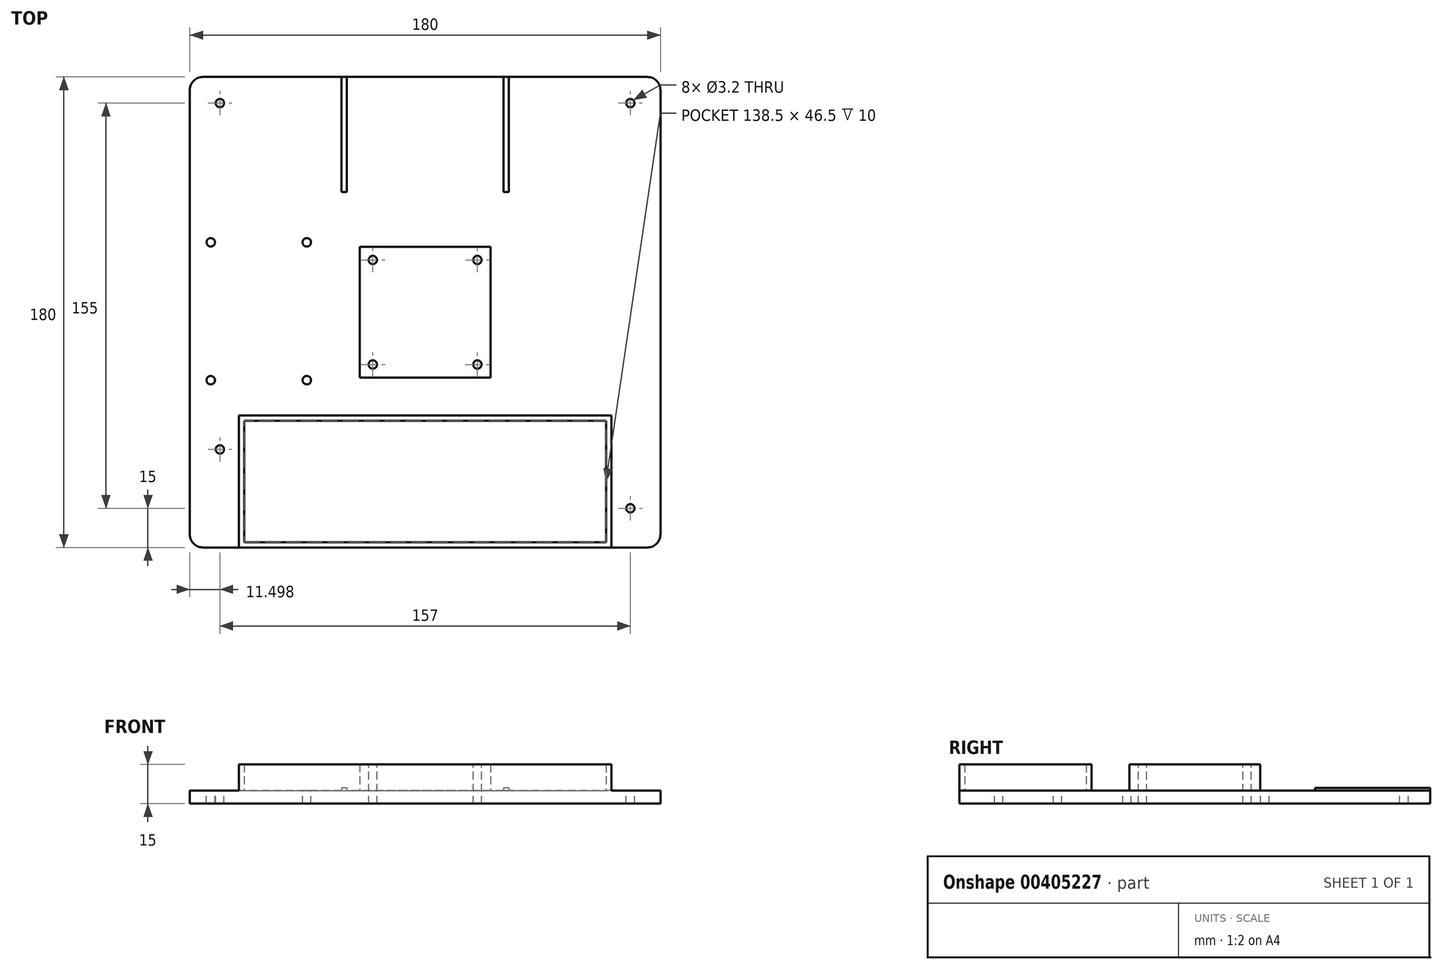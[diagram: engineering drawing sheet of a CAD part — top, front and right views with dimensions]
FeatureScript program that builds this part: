
annotation { "Feature Type Name" : "Feature", "Feature Type Description" : "" }
export const myFeature = defineFeature(function(context is Context, id is Id, definition is map)
    precondition{}
    {
        {
            var Q0;
            Q0=qCreatedBy(makeId("Top.planeOp"),FACE);
            var sketch = newSketch(context, id + "F0", { "sketchPlane" : qUnion([Q0])});
            skLineSegment(sketch, "E0.bottom", {"start": v(87.98, 0) * mm, "end": v(-92.02, 0) * mm});
            skLineSegment(sketch, "E0.top", {"start": v(87.98, 180) * mm, "end": v(-92.02, 180) * mm});
            skLineSegment(sketch, "E0.left", {"start": v(87.98, 0) * mm, "end": v(87.98, 180) * mm});
            skLineSegment(sketch, "E0.right", {"start": v(-92.02, 0) * mm, "end": v(-92.02, 180) * mm});
            skSolve(sketch);
        }
        {
            var Q0;
            Q0=makeQuery(id+"F0.imprint","IMPRINT",FACE,{"disambiguationData":[TD([[makeQuery(id+"F0.imprint","IMPRINT",EDGE,{"derivedFrom":sQuery(id+"F0.wireOp",EDGE,"E0.bottom")}),-1.0]])]});
            extrude(context, id + "F1", {"entities" : qUnion([Q0]), "depth" : 5 * mm});
        }
        {
            var Q0;
            Q0=makeQuery(id+"F1.opExtrude","SWEPT_EDGE",EDGE,{"disambiguationData":[OSD([sQuery(id+"F0.wireOp",EDGE,"E0.bottom"),sQuery(id+"F0.wireOp",EDGE,"E0.left")])]});
            var Q1;
            Q1=makeQuery(id+"F1.opExtrude","SWEPT_EDGE",EDGE,{"disambiguationData":[OSD([sQuery(id+"F0.wireOp",EDGE,"E0.top"),sQuery(id+"F0.wireOp",EDGE,"E0.right")])]});
            var Q2;
            Q2=makeQuery(id+"F1.opExtrude","SWEPT_EDGE",EDGE,{"disambiguationData":[OSD([sQuery(id+"F0.wireOp",EDGE,"E0.bottom"),sQuery(id+"F0.wireOp",EDGE,"E0.right")])]});
            var Q3;
            Q3=makeQuery(id+"F1.opExtrude","SWEPT_EDGE",EDGE,{"disambiguationData":[OSD([sQuery(id+"F0.wireOp",EDGE,"E0.top"),sQuery(id+"F0.wireOp",EDGE,"E0.left")])]});
            fillet(context, id + "F2", {"entities" : qUnion([Q0, Q1, Q2, Q3]), "radius" : 5 * mm, "tangentPropagation" : true, "allowEdgeOverflow" : false});
        }
        {
            var Q0;
            Q0=makeQuery(id+"F1.opExtrude","CAP_FACE",FACE,{"disambiguationData":[OSD([sQuery(id+"F0.wireOp",EDGE,"E0.bottom"),sQuery(id+"F0.wireOp",EDGE,"E0.top"),sQuery(id+"F0.wireOp",EDGE,"E0.left"),sQuery(id+"F0.wireOp",EDGE,"E0.right")])],"isStart":false});
            var sketch = newSketch(context, id + "F3", { "sketchPlane" : qUnion([Q0])});
            skCircle(sketch, "E1", {"center": v(-80.52, 170) * mm, "radius": 1.6 * mm});
            skCircle(sketch, "E2", {"center": v(76.48, 170) * mm, "radius": 1.6 * mm});
            skCircle(sketch, "E3", {"center": v(76.48, 15) * mm, "radius": 1.6 * mm});
            skCircle(sketch, "E4", {"center": v(-80.52, 37.5) * mm, "radius": 1.6 * mm});
            skSolve(sketch);
        }
        {
            var Q0;
            Q0 = qSketchRegion(id + "F3", true);
            extrude(context, id + "F4", {"entities" : qUnion([Q0]), "operationType" : NewBodyOperationType.REMOVE, "oppositeDirection" : true, "depth" : 5 * mm});
        }
        {
            var Q0;
            Q0=makeQuery(id+"F1.opExtrude","CAP_FACE",FACE,{"disambiguationData":[OSD([sQuery(id+"F0.wireOp",EDGE,"E0.bottom"),sQuery(id+"F0.wireOp",EDGE,"E0.top"),sQuery(id+"F0.wireOp",EDGE,"E0.left"),sQuery(id+"F0.wireOp",EDGE,"E0.right")])],"isStart":false});
            var sketch = newSketch(context, id + "F5", { "sketchPlane" : qUnion([Q0])});
            skCircle(sketch, "E5", {"center": v(-84.02, 64) * mm, "radius": 1.63 * mm});
            skCircle(sketch, "E6", {"center": v(-84.02, 116.75) * mm, "radius": 1.63 * mm});
            skCircle(sketch, "E7", {"center": v(-47.27, 64) * mm, "radius": 1.63 * mm});
            skCircle(sketch, "E8", {"center": v(-47.27, 116.75) * mm, "radius": 1.63 * mm});
            skSolve(sketch);
        }
        {
            var Q0;
            Q0 = qSketchRegion(id + "F5", true);
            extrude(context, id + "F6", {"entities" : qUnion([Q0]), "operationType" : NewBodyOperationType.REMOVE, "oppositeDirection" : true, "depth" : 5 * mm});
        }
        {
            var Q0;
            Q0=makeQuery(id+"F1.opExtrude","CAP_FACE",FACE,{"disambiguationData":[OSD([sQuery(id+"F0.wireOp",EDGE,"E0.bottom"),sQuery(id+"F0.wireOp",EDGE,"E0.top"),sQuery(id+"F0.wireOp",EDGE,"E0.left"),sQuery(id+"F0.wireOp",EDGE,"E0.right")])],"isStart":false});
            var sketch = newSketch(context, id + "F7", { "sketchPlane" : qUnion([Q0])});
            skPoint(sketch, "E9.middle", {"position": v(-2.02, 90) * mm});
            skPoint(sketch, "E9.middle.positionSnap0", {"position": v(-92.02, 90) * mm});
            skPoint(sketch, "E9.centerSnap0", {"position": v(-92.02, 90) * mm});
            skLineSegment(sketch, "E10.bottom", {"start": v(22.98, 115) * mm, "end": v(-27.02, 115) * mm});
            skLineSegment(sketch, "E10.top", {"start": v(22.98, 65) * mm, "end": v(-27.02, 65) * mm});
            skLineSegment(sketch, "E10.left", {"start": v(22.98, 115) * mm, "end": v(22.98, 65) * mm});
            skLineSegment(sketch, "E10.right", {"start": v(-27.02, 115) * mm, "end": v(-27.02, 65) * mm});
            skSolve(sketch);
        }
        {
            var Q0;
            Q0 = qSketchRegion(id + "F7", true);
            extrude(context, id + "F8", {"entities" : qUnion([Q0]), "operationType" : NewBodyOperationType.ADD, "depth" : 10 * mm});
        }
        {
            var Q0;
            Q0=makeQuery(id+"F8.opExtrude","CAP_FACE",FACE,{"disambiguationData":[OSD([sQuery(id+"F7.wireOp",EDGE,"E10.bottom"),sQuery(id+"F7.wireOp",EDGE,"E10.top"),sQuery(id+"F7.wireOp",EDGE,"E10.left"),sQuery(id+"F7.wireOp",EDGE,"E10.right")])],"isStart":false});
            var sketch = newSketch(context, id + "F9", { "sketchPlane" : qUnion([Q0])});
            skCircle(sketch, "E11", {"center": v(-22.02, 70) * mm, "radius": 1.6 * mm});
            skCircle(sketch, "E12.1.0", {"center": v(17.98, 70) * mm, "radius": 1.6 * mm});
            skCircle(sketch, "E12.2.0", {"center": v(17.98, 110) * mm, "radius": 1.6 * mm});
            skCircle(sketch, "E12.3.0", {"center": v(-22.02, 110) * mm, "radius": 1.6 * mm});
            skPoint(sketch, "E12.center", {"position": v(-2.02, 90) * mm});
            skSolve(sketch);
        }
        {
            var Q0;
            Q0=makeQuery(id+"F1.opExtrude","CAP_FACE",FACE,{"disambiguationData":[OSD([sQuery(id+"F0.wireOp",EDGE,"E0.bottom"),sQuery(id+"F0.wireOp",EDGE,"E0.top"),sQuery(id+"F0.wireOp",EDGE,"E0.left"),sQuery(id+"F0.wireOp",EDGE,"E0.right")])],"isStart":false});
            var sketch = newSketch(context, id + "F10", { "sketchPlane" : qUnion([Q0])});
            skPoint(sketch, "E13.middle", {"position": v(0, 25.25) * mm});
            skLineSegment(sketch, "E14", {"start": v(-2.02, 25.25) * mm, "end": v(-2.02, 154.04) * mm});
            skLineSegment(sketch, "E15.bottom", {"start": v(-71.27, 48.5) * mm, "end": v(67.23, 48.5) * mm});
            skLineSegment(sketch, "E15.top", {"start": v(-71.27, 2) * mm, "end": v(67.23, 2) * mm});
            skLineSegment(sketch, "E15.left", {"start": v(-71.27, 48.5) * mm, "end": v(-71.27, 2) * mm});
            skLineSegment(sketch, "E15.right", {"start": v(67.23, 48.5) * mm, "end": v(67.23, 2) * mm});
            skPoint(sketch, "E15.middle", {"position": v(-2.02, 25.25) * mm});
            skLineSegment(sketch, "E16.0", {"start": v(-73.27, 50.5) * mm, "end": v(69.23, 50.5) * mm});
            skLineSegment(sketch, "E16.1", {"start": v(-73.27, 50.5) * mm, "end": v(-73.27, 0) * mm});
            skLineSegment(sketch, "E16.2", {"start": v(-73.27, 0) * mm, "end": v(69.23, 0) * mm});
            skLineSegment(sketch, "E16.3", {"start": v(69.23, 50.5) * mm, "end": v(69.23, 0) * mm});
            skSolve(sketch);
        }
        {
            var Q0;
            Q0 = qSketchRegion(id + "F10", true);
            extrude(context, id + "F11", {"entities" : qUnion([Q0]), "operationType" : NewBodyOperationType.ADD, "depth" : 10 * mm});
        }
        {
            var Q0;
            Q0 = qSketchRegion(id + "F9", true);
            extrude(context, id + "F12", {"entities" : qUnion([Q0]), "operationType" : NewBodyOperationType.REMOVE, "oppositeDirection" : true, "depth" : 25 * mm});
        }
        {
            var Q0;
            {var subQ0=sQuery(id+"F0.wireOp",EDGE,"E0.bottom");var subQ1=sQuery(id+"F0.wireOp",EDGE,"E0.left");var subQ2=sQuery(id+"F0.wireOp",EDGE,"E0.top");var subQ3=sQuery(id+"F0.wireOp",EDGE,"E0.right");Q0=makeQuery(id+"F11.boolean.opBoolean","SPLIT",FACE,{"disambiguationData":[TD([makeQuery(id+"F1.opExtrude","SWEPT_FACE",FACE,{"disambiguationData":[OSD([subQ0])]})])],"derivedFrom":makeQuery(id+"F1.opExtrude","CAP_FACE",FACE,{"disambiguationData":[OSD([subQ0,subQ2,subQ1,subQ3])],"isStart":false})});}
            var sketch = newSketch(context, id + "F13", { "sketchPlane" : qUnion([Q0])});
            skLineSegment(sketch, "E17", {"start": v(-92.02, 175) * mm, "end": v(-2.02, 175) * mm, "construction": true});
            skLineSegment(sketch, "E18", {"start": v(-2.02, 175) * mm, "end": v(-2.02, 53.3) * mm, "construction": true});
            skPoint(sketch, "E18.endSnap0", {"position": v(-2.02, 65) * mm});
            skLineSegment(sketch, "E19", {"start": v(-32.02, 180) * mm, "end": v(-32.02, 136) * mm});
            skLineSegment(sketch, "E20.0", {"start": v(-34.02, 180) * mm, "end": v(-34.02, 136) * mm});
            skLineSegment(sketch, "E21", {"start": v(-34.02, 136) * mm, "end": v(-32.02, 136) * mm});
            skLineSegment(sketch, "E22", {"start": v(-34.02, 180) * mm, "end": v(-32.02, 180) * mm});
            skLineSegment(sketch, "E23.MirrorCS", {"start": v(29.98, 136) * mm, "end": v(27.98, 136) * mm});
            skLineSegment(sketch, "E24.MirrorCS", {"start": v(29.98, 180) * mm, "end": v(27.98, 180) * mm});
            skLineSegment(sketch, "E25.MirrorCS", {"start": v(29.98, 180) * mm, "end": v(29.98, 136) * mm});
            skLineSegment(sketch, "E26.MirrorCS", {"start": v(27.98, 180) * mm, "end": v(27.98, 136) * mm});
            skSolve(sketch);
        }
        {
            var Q0;
            Q0 = qSketchRegion(id + "F13", true);
            extrude(context, id + "F14", {"entities" : qUnion([Q0]), "operationType" : NewBodyOperationType.ADD, "depth" : 1 * mm});
        }
    });
